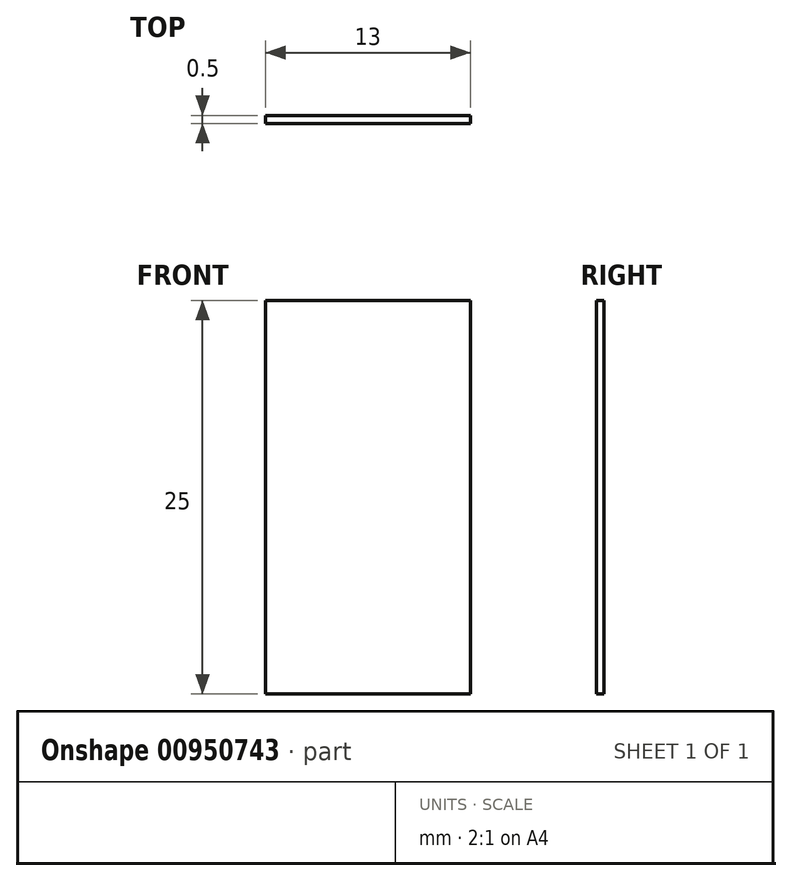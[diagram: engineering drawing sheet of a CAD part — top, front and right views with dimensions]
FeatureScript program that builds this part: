
annotation { "Feature Type Name" : "Feature", "Feature Type Description" : "" }
export const myFeature = defineFeature(function(context is Context, id is Id, definition is map)
    precondition{}
    {
        {
            var Q0;
            Q0=qCreatedBy(makeId("Front.planeOp"),FACE);
            var sketch = newSketch(context, id + "F0", { "sketchPlane" : qUnion([Q0])});
            skLineSegment(sketch, "E0.bottom", {"start": v(-6.5, 0) * mm, "end": v(6.5, 0) * mm});
            skLineSegment(sketch, "E0.top", {"start": v(-6.5, 25) * mm, "end": v(6.5, 25) * mm});
            skLineSegment(sketch, "E0.left", {"start": v(-6.5, 0) * mm, "end": v(-6.5, 25) * mm});
            skLineSegment(sketch, "E0.right", {"start": v(6.5, 0) * mm, "end": v(6.5, 25) * mm});
            skLineSegment(sketch, "E1.bottom", {"start": v(-2.95, 0) * mm, "end": v(-2.15, 0) * mm});
            skLineSegment(sketch, "E1.top", {"start": v(-2.95, -5.1) * mm, "end": v(-2.15, -5.1) * mm});
            skLineSegment(sketch, "E1.left", {"start": v(-2.95, 0) * mm, "end": v(-2.95, -5.1) * mm});
            skLineSegment(sketch, "E1.right", {"start": v(-2.15, 0) * mm, "end": v(-2.15, -5.1) * mm});
            skLineSegment(sketch, "E2.bottom", {"start": v(2.15, 0) * mm, "end": v(2.95, 0) * mm});
            skLineSegment(sketch, "E2.top", {"start": v(2.15, -5.1) * mm, "end": v(2.95, -5.1) * mm});
            skLineSegment(sketch, "E2.left", {"start": v(2.15, 0) * mm, "end": v(2.15, -5.1) * mm});
            skLineSegment(sketch, "E2.right", {"start": v(2.95, 0) * mm, "end": v(2.95, -5.1) * mm});
            skPoint(sketch, "E3", {"position": v(0, 0) * mm});
            skPoint(sketch, "E4", {"position": v(-2.55, -5.1) * mm});
            skPoint(sketch, "E5", {"position": v(2.55, -5.1) * mm});
            skLineSegment(sketch, "E6.bottom", {"start": v(-5.1, 23.5) * mm, "end": v(5.1, 23.5) * mm, "construction": true});
            skLineSegment(sketch, "E6.top", {"start": v(-5.1, 1.5) * mm, "end": v(5.1, 1.5) * mm, "construction": true});
            skLineSegment(sketch, "E6.left", {"start": v(-5.1, 23.5) * mm, "end": v(-5.1, 1.5) * mm, "construction": true});
            skLineSegment(sketch, "E6.right", {"start": v(5.1, 23.5) * mm, "end": v(5.1, 1.5) * mm, "construction": true});
            skPoint(sketch, "E7", {"position": v(0, 23.5) * mm});
            skPoint(sketch, "E8", {"position": v(-5.1, 12.5) * mm});
            skPoint(sketch, "E9", {"position": v(-6.5, 12.5) * mm});
            skPoint(sketch, "E10", {"position": v(0, 25) * mm});
            skSolve(sketch);
        }
        {
            var Q0;
            Q0=makeQuery(id+"F0.imprint","IMPRINT",FACE,{"disambiguationData":[TD([[makeQuery(id+"F0.imprint","IMPRINT",EDGE,{"derivedFrom":sQuery(id+"F0.wireOp",EDGE,"E0.top")}),-1.0]])]});
            var Q1;
            Q1=makeQuery(id+"F0.imprint","IMPRINT",FACE,{"disambiguationData":[TD([[makeQuery(id+"F0.imprint","IMPRINT",EDGE,{"derivedFrom":sQuery(id+"F0.wireOp",EDGE,"E1.bottom")}),-1.0]])]});
            var Q2;
            Q2=makeQuery(id+"F0.imprint","IMPRINT",FACE,{"disambiguationData":[TD([[makeQuery(id+"F0.imprint","IMPRINT",EDGE,{"derivedFrom":sQuery(id+"F0.wireOp",EDGE,"E2.bottom")}),-1.0]])]});
            extrude(context, id + "F1", {"entities" : qUnion([Q0, Q1, Q2]), "depth" : 0.5 * mm, "offsetDistance" : 25 * mm});
        }
    });
